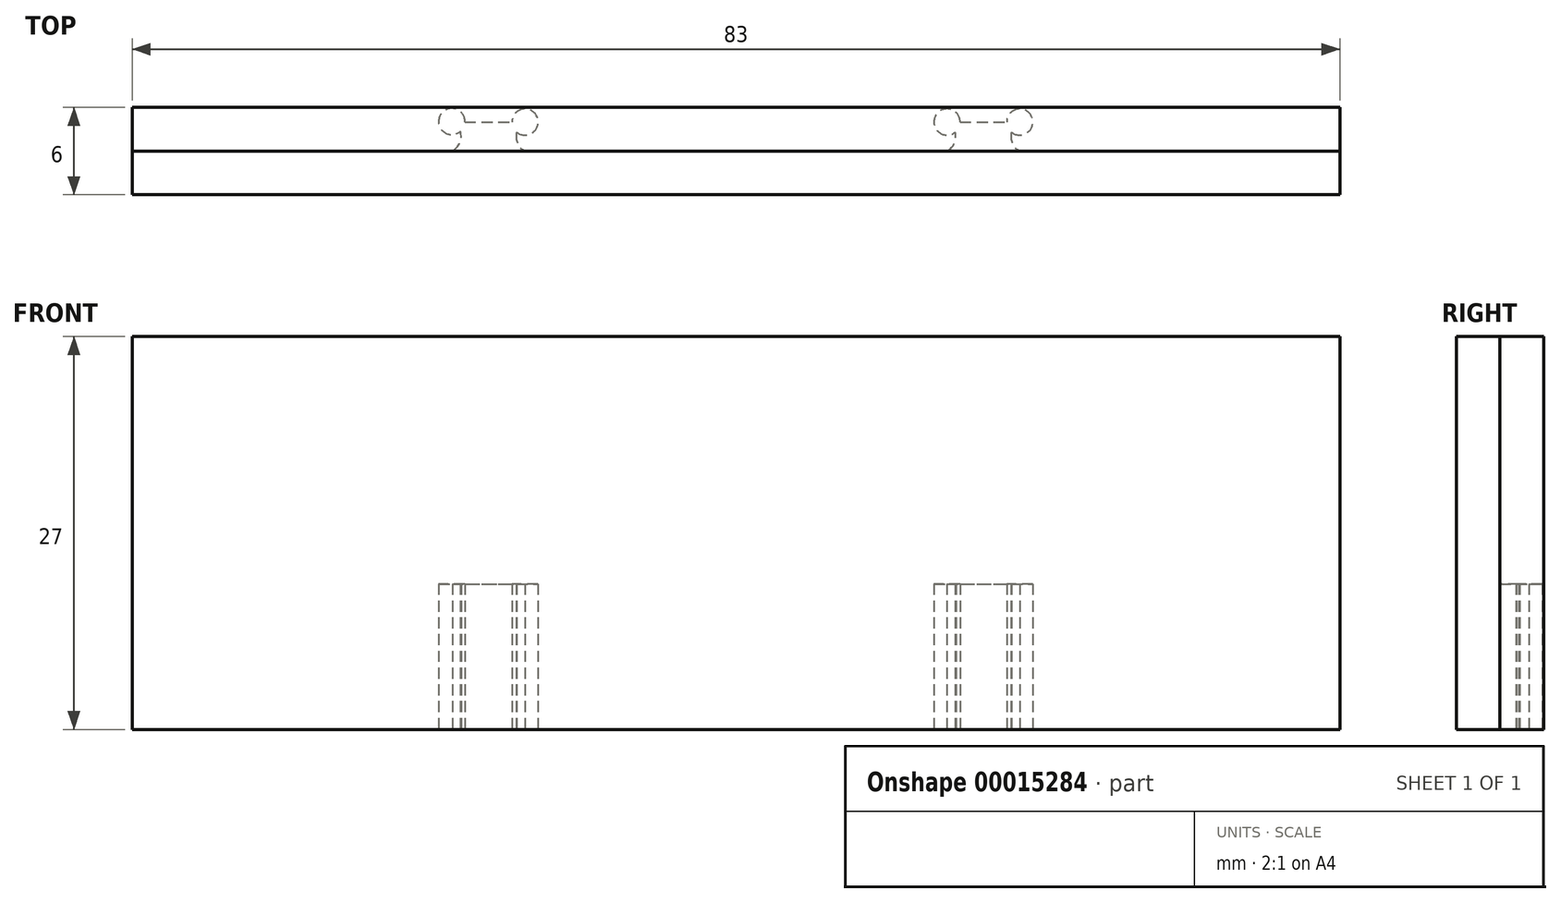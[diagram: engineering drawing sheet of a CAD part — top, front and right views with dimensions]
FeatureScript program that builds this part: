
annotation { "Feature Type Name" : "Feature", "Feature Type Description" : "" }
export const myFeature = defineFeature(function(context is Context, id is Id, definition is map)
    precondition{}
    {
        {
            var Q0;
            Q0=qCreatedBy(makeId("Top.planeOp"),FACE);
            var sketch = newSketch(context, id + "F0", { "sketchPlane" : qUnion([Q0])});
            skLineSegment(sketch, "E0.bottom", {"start": v(0, 0) * mm, "end": v(24.5, 0) * mm});
            skLineSegment(sketch, "E0.top", {"start": v(0, -3) * mm, "end": v(83, -3) * mm});
            skLineSegment(sketch, "E0.left", {"start": v(0, 0) * mm, "end": v(0, -3) * mm});
            skLineSegment(sketch, "E0.right", {"start": v(83, 0) * mm, "end": v(83, -3) * mm});
            skLineSegment(sketch, "E1", {"start": v(0, 2) * mm, "end": v(24.5, 2) * mm, "construction": true});
            skLineSegment(sketch, "E2", {"start": v(24.5, 2) * mm, "end": v(24.5, 0) * mm, "construction": true});
            skLineSegment(sketch, "E3", {"start": v(24.5, 2) * mm, "end": v(27, 2) * mm});
            skLineSegment(sketch, "E4.trimOffspring", {"start": v(27, 0) * mm, "end": v(83, 0) * mm});
            skLineSegment(sketch, "E5", {"start": v(24.5, 0) * mm, "end": v(27, 0) * mm});
            skLineSegment(sketch, "E6.MirrorCS", {"start": v(24.5, 2) * mm, "end": v(22, 2) * mm});
            skLineSegment(sketch, "E7.MirrorCS", {"start": v(24.5, 0) * mm, "end": v(22, 0) * mm});
            skLineSegment(sketch, "E8", {"start": v(83, 2) * mm, "end": v(58.5, 2) * mm, "construction": true});
            skLineSegment(sketch, "E9.1.0.0", {"start": v(58.5, 0) * mm, "end": v(61, 0) * mm});
            skLineSegment(sketch, "E9.1.0.2", {"start": v(58.5, 2) * mm, "end": v(56, 2) * mm});
            skLineSegment(sketch, "E9.1.0.3", {"start": v(58.5, 0) * mm, "end": v(56, 0) * mm});
            skLineSegment(sketch, "E9.1.0.4", {"start": v(58.5, 2) * mm, "end": v(61, 2) * mm});
            skLineSegment(sketch, "E9.1.0.6", {"start": v(58.5, 2) * mm, "end": v(58.5, 0) * mm, "construction": true});
            skLineSegment(sketch, "E9.direction1", {"start": v(24.5, 0) * mm, "end": v(58.5, 0) * mm, "construction": true});
            skLineSegment(sketch, "E10.bottom", {"start": v(0, -3) * mm, "end": v(7.5, -3) * mm});
            skLineSegment(sketch, "E10.top", {"start": v(0, -19) * mm, "end": v(7.5, -19) * mm});
            skLineSegment(sketch, "E10.left", {"start": v(0, -3) * mm, "end": v(0, -19) * mm});
            skLineSegment(sketch, "E10.right", {"start": v(7.5, -3) * mm, "end": v(7.5, -19) * mm});
            skLineSegment(sketch, "E11.bottom", {"start": v(83, -3) * mm, "end": v(75.5, -3) * mm});
            skLineSegment(sketch, "E11.top", {"start": v(83, -19) * mm, "end": v(75.5, -19) * mm});
            skLineSegment(sketch, "E11.left", {"start": v(83, -3) * mm, "end": v(83, -19) * mm});
            skLineSegment(sketch, "E11.right", {"start": v(75.5, -3) * mm, "end": v(75.5, -19) * mm});
            skArc(sketch, "E12", {"start": v(22, 0) * mm, "mid": v(22.6, 1) * mm, "end": v(22, 2) * mm});
            skArc(sketch, "E13.MirrorCS", {"start": v(27, 0) * mm, "mid": v(26.4, 1) * mm, "end": v(27, 2) * mm});
            skArc(sketch, "E14", {"start": v(56, 0) * mm, "mid": v(56.6, 1) * mm, "end": v(56, 2) * mm});
            skArc(sketch, "E15.MirrorCS", {"start": v(61, 0) * mm, "mid": v(60.4, 1) * mm, "end": v(61, 2) * mm});
            skSolve(sketch);
        }
        {
            var Q0;
            Q0=qCreatedBy(makeId("Top.planeOp"),FACE);
            var sketch = newSketch(context, id + "F1", { "sketchPlane" : qUnion([Q0])});
            skLineSegment(sketch, "E16.bottom", {"start": v(0, 0) * mm, "end": v(83, 0) * mm});
            skLineSegment(sketch, "E16.top", {"start": v(0, 3) * mm, "end": v(83, 3) * mm});
            skLineSegment(sketch, "E16.left", {"start": v(0, 0) * mm, "end": v(0, 3) * mm});
            skLineSegment(sketch, "E16.right", {"start": v(83, 0) * mm, "end": v(83, 3) * mm});
            skLineSegment(sketch, "E17.0", {"start": v(24.5, 2) * mm, "end": v(22.87, 2) * mm});
            skLineSegment(sketch, "E18.0", {"start": v(24.5, 2) * mm, "end": v(26.1, 2) * mm});
            skLineSegment(sketch, "E19.0", {"start": v(58.5, 2) * mm, "end": v(56.9, 2) * mm});
            skLineSegment(sketch, "E20.0", {"start": v(58.5, 2) * mm, "end": v(60.1, 2) * mm});
            skCircle(sketch, "E21", {"center": v(21.97, 2.04) * mm, "radius": 0.9 * mm});
            skCircle(sketch, "E22", {"center": v(27, 2) * mm, "radius": 0.9 * mm});
            skCircle(sketch, "E23", {"center": v(56, 2) * mm, "radius": 0.9 * mm});
            skCircle(sketch, "E24", {"center": v(61, 2) * mm, "radius": 0.9 * mm});
            skArc(sketch, "E25.0", {"start": v(22, 0) * mm, "mid": v(22.52, 0.58) * mm, "end": v(22.55, 1.35) * mm});
            skArc(sketch, "E26.0", {"start": v(27, 0) * mm, "mid": v(26.49, 0.55) * mm, "end": v(26.43, 1.3) * mm});
            skArc(sketch, "E27.0", {"start": v(56, 0) * mm, "mid": v(56.51, 0.55) * mm, "end": v(56.57, 1.3) * mm});
            skArc(sketch, "E28.0", {"start": v(61, 0) * mm, "mid": v(60.49, 0.55) * mm, "end": v(60.43, 1.3) * mm});
            skPoint(sketch, "E29.orphan", {"position": v(22, 2) * mm});
            skSolve(sketch);
        }
        {
            var Q0;
            Q0=makeQuery(id+"F0.imprint","IMPRINT",FACE,{"disambiguationData":[TD([[makeQuery(id+"F0.imprint","IMPRINT",EDGE,{"derivedFrom":sQuery(id+"F0.wireOp",EDGE,"E0.bottom")}),-1.0]])]});
            var Q1;
            Q1=makeQuery(id+"F0.imprint","IMPRINT",FACE,{"disambiguationData":[TD([[makeQuery(id+"F0.imprint","IMPRINT",EDGE,{"derivedFrom":sQuery(id+"F0.wireOp",EDGE,"E11.bottom")}),1.0]])]});
            var Q2;
            Q2=makeQuery(id+"F0.imprint","IMPRINT",FACE,{"disambiguationData":[TD([[makeQuery(id+"F0.imprint","IMPRINT",EDGE,{"derivedFrom":sQuery(id+"F0.wireOp",EDGE,"E10.bottom")}),-1.0]])]});
            extrude(context, id + "F2", {"entities" : qUnion([Q0, Q1, Q2]), "depth" : 27 * mm});
        }
        {
            var Q0;
            Q0=makeQuery(id+"F0.imprint","IMPRINT",FACE,{"disambiguationData":[TD([[makeQuery(id+"F0.imprint","IMPRINT",EDGE,{"derivedFrom":sQuery(id+"F0.wireOp",EDGE,"E9.1.0.0")}),1.0]])]});
            var Q1;
            Q1=makeQuery(id+"F0.imprint","IMPRINT",FACE,{"disambiguationData":[TD([[makeQuery(id+"F0.imprint","IMPRINT",EDGE,{"derivedFrom":sQuery(id+"F0.wireOp",EDGE,"E3")}),-1.0]])]});
            extrude(context, id + "F3", {"entities" : qUnion([Q0, Q1]), "operationType" : NewBodyOperationType.ADD, "depth" : 10 * mm});
        }
        {
            var Q0;
            Q0 = qSketchRegion(id + "F1", true);
            var Q1;
            {var subQ1=sQuery(id+"F1.wireOp",EDGE,"6b6c7125-87d3-4553-a127-3a18f75b3079.0");var subQ3=sQuery(id+"F1.wireOp",EDGE,"E18.0");var subQ5=makeQuery(id+"F1.imprint","INTERSECT",VERTEX,{"derivedFrom":[subQ3,subQ1]});Q1=makeQuery(id+"F1.imprint","IMPRINT",FACE,{"disambiguationData":[TD([[makeQuery(id+"F1.imprint","IMPRINT",EDGE,{"disambiguationData":[TD([[subQ5,1.0]])],"derivedFrom":subQ3}),1.0]])]});}
            var Q2;
            {var subQ1=sQuery(id+"F1.wireOp",EDGE,"6b6c7125-87d3-4553-a127-3a18f75b3079.0");var subQ3=sQuery(id+"F1.wireOp",EDGE,"E18.0");var subQ5=makeQuery(id+"F1.imprint","INTERSECT",VERTEX,{"derivedFrom":[subQ3,subQ1]});Q2=makeQuery(id+"F1.imprint","IMPRINT",FACE,{"disambiguationData":[TD([[makeQuery(id+"F1.imprint","IMPRINT",EDGE,{"disambiguationData":[TD([[subQ5,1.0]])],"derivedFrom":subQ3}),-1.0]])]});}
            var Q3;
            {var subQ1=sQuery(id+"F1.wireOp",EDGE,"E17.0");var subQ3=sQuery(id+"F1.wireOp",EDGE,"38192091-4c4b-4ebf-abf7-9709ffb2822d.0");var subQ5=makeQuery(id+"F1.imprint","INTERSECT",VERTEX,{"derivedFrom":[subQ3,subQ1]});Q3=makeQuery(id+"F1.imprint","IMPRINT",FACE,{"disambiguationData":[TD([[makeQuery(id+"F1.imprint","IMPRINT",EDGE,{"disambiguationData":[TD([[subQ5,-1.0]])],"derivedFrom":subQ3}),-1.0]])]});}
            var Q4;
            {var subQ1=sQuery(id+"F1.wireOp",EDGE,"E17.0");var subQ3=sQuery(id+"F1.wireOp",EDGE,"38192091-4c4b-4ebf-abf7-9709ffb2822d.0");var subQ5=makeQuery(id+"F1.imprint","INTERSECT",VERTEX,{"derivedFrom":[subQ3,subQ1]});Q4=makeQuery(id+"F1.imprint","IMPRINT",FACE,{"disambiguationData":[TD([[makeQuery(id+"F1.imprint","IMPRINT",EDGE,{"disambiguationData":[TD([[subQ5,-1.0]])],"derivedFrom":subQ3}),1.0]])]});}
            var Q5;
            {var subQ1=sQuery(id+"F1.wireOp",EDGE,"e493a4b6-5bd2-4034-9364-0e4b5c8cb8ea.0");var subQ3=sQuery(id+"F1.wireOp",EDGE,"E19.0");var subQ5=makeQuery(id+"F1.imprint","INTERSECT",VERTEX,{"derivedFrom":[subQ3,subQ1]});Q5=makeQuery(id+"F1.imprint","IMPRINT",FACE,{"disambiguationData":[TD([[makeQuery(id+"F1.imprint","IMPRINT",EDGE,{"disambiguationData":[TD([[subQ5,1.0]])],"derivedFrom":subQ3}),-1.0]])]});}
            var Q6;
            {var subQ1=sQuery(id+"F1.wireOp",EDGE,"e493a4b6-5bd2-4034-9364-0e4b5c8cb8ea.0");var subQ3=sQuery(id+"F1.wireOp",EDGE,"E19.0");var subQ5=makeQuery(id+"F1.imprint","INTERSECT",VERTEX,{"derivedFrom":[subQ3,subQ1]});Q6=makeQuery(id+"F1.imprint","IMPRINT",FACE,{"disambiguationData":[TD([[makeQuery(id+"F1.imprint","IMPRINT",EDGE,{"disambiguationData":[TD([[subQ5,1.0]])],"derivedFrom":subQ3}),1.0]])]});}
            var Q7;
            {var subQ1=sQuery(id+"F1.wireOp",EDGE,"c7cf41aa-584b-4ac6-8513-ffaf11a8ccd2.0");var subQ3=sQuery(id+"F1.wireOp",EDGE,"E20.0");var subQ5=makeQuery(id+"F1.imprint","INTERSECT",VERTEX,{"derivedFrom":[subQ3,subQ1]});Q7=makeQuery(id+"F1.imprint","IMPRINT",FACE,{"disambiguationData":[TD([[makeQuery(id+"F1.imprint","IMPRINT",EDGE,{"disambiguationData":[TD([[subQ5,1.0]])],"derivedFrom":subQ3}),1.0]])]});}
            var Q8;
            {var subQ1=sQuery(id+"F1.wireOp",EDGE,"c7cf41aa-584b-4ac6-8513-ffaf11a8ccd2.0");var subQ3=sQuery(id+"F1.wireOp",EDGE,"E20.0");var subQ5=makeQuery(id+"F1.imprint","INTERSECT",VERTEX,{"derivedFrom":[subQ3,subQ1]});Q8=makeQuery(id+"F1.imprint","IMPRINT",FACE,{"disambiguationData":[TD([[makeQuery(id+"F1.imprint","IMPRINT",EDGE,{"disambiguationData":[TD([[subQ5,1.0]])],"derivedFrom":subQ3}),-1.0]])]});}
            var Q9;
            {var subQ0=sQuery(id+"F1.wireOp",EDGE,"E25.0");var subQ3=sQuery(id+"F1.wireOp",EDGE,"E17.0");var subQ4=makeQuery(id+"F1.imprint","INTERSECT",VERTEX,{"derivedFrom":[subQ3,subQ0]});Q9=makeQuery(id+"F1.imprint","IMPRINT",FACE,{"disambiguationData":[TD([[makeQuery(id+"F1.imprint","IMPRINT",EDGE,{"disambiguationData":[TD([[subQ4,1.0]])],"derivedFrom":subQ3}),-1.0]])]});}
            var Q10;
            {var subQ0=sQuery(id+"F1.wireOp",EDGE,"E23");var subQ2=makeQuery(id+"F1.imprint","INTERSECT",VERTEX,{"derivedFrom":[sQuery(id+"F1.wireOp",EDGE,"E19.0"),subQ0]});Q10=makeQuery(id+"F1.imprint","IMPRINT",FACE,{"disambiguationData":[TD([[makeQuery(id+"F1.imprint","IMPRINT",EDGE,{"disambiguationData":[TD([[subQ2,-1.0]])],"derivedFrom":subQ0}),1.0]])]});}
            var Q11;
            {var subQ0=sQuery(id+"F1.wireOp",EDGE,"E24");var subQ2=makeQuery(id+"F1.imprint","INTERSECT",VERTEX,{"derivedFrom":[sQuery(id+"F1.wireOp",EDGE,"E20.0"),subQ0]});Q11=makeQuery(id+"F1.imprint","IMPRINT",FACE,{"disambiguationData":[TD([[makeQuery(id+"F1.imprint","IMPRINT",EDGE,{"disambiguationData":[TD([[subQ2,-1.0]])],"derivedFrom":subQ0}),1.0]])]});}
            var Q12;
            {var subQ0=sQuery(id+"F1.wireOp",EDGE,"E21");var subQ2=makeQuery(id+"F1.imprint","INTERSECT",VERTEX,{"derivedFrom":[sQuery(id+"F1.wireOp",EDGE,"E17.0"),subQ0]});Q12=makeQuery(id+"F1.imprint","IMPRINT",FACE,{"disambiguationData":[TD([[makeQuery(id+"F1.imprint","IMPRINT",EDGE,{"disambiguationData":[TD([[subQ2,-1.0]])],"derivedFrom":subQ0}),1.0]])]});}
            var Q13;
            {var subQ0=sQuery(id+"F1.wireOp",EDGE,"E22");var subQ2=makeQuery(id+"F1.imprint","INTERSECT",VERTEX,{"derivedFrom":[sQuery(id+"F1.wireOp",EDGE,"E18.0"),subQ0]});Q13=makeQuery(id+"F1.imprint","IMPRINT",FACE,{"disambiguationData":[TD([[makeQuery(id+"F1.imprint","IMPRINT",EDGE,{"disambiguationData":[TD([[subQ2,-1.0]])],"derivedFrom":subQ0}),1.0]])]});}
            extrude(context, id + "F4", {"entities" : qUnion([Q0, Q1, Q2, Q3, Q4, Q5, Q6, Q7, Q8, Q9, Q10, Q11, Q12, Q13]), "depth" : 27 * mm});
        }
        {
            var Q0;
            {var subQ0=sQuery(id+"F1.wireOp",EDGE,"E23");var subQ2=makeQuery(id+"F1.imprint","INTERSECT",VERTEX,{"derivedFrom":[sQuery(id+"F1.wireOp",EDGE,"E19.0"),subQ0]});Q0=makeQuery(id+"F1.imprint","IMPRINT",FACE,{"disambiguationData":[TD([[makeQuery(id+"F1.imprint","IMPRINT",EDGE,{"disambiguationData":[TD([[subQ2,-1.0]])],"derivedFrom":subQ0}),1.0]])]});}
            var Q1;
            {var subQ0=sQuery(id+"F1.wireOp",EDGE,"E24");var subQ2=makeQuery(id+"F1.imprint","INTERSECT",VERTEX,{"derivedFrom":[sQuery(id+"F1.wireOp",EDGE,"E20.0"),subQ0]});Q1=makeQuery(id+"F1.imprint","IMPRINT",FACE,{"disambiguationData":[TD([[makeQuery(id+"F1.imprint","IMPRINT",EDGE,{"disambiguationData":[TD([[subQ2,-1.0]])],"derivedFrom":subQ0}),1.0]])]});}
            var Q2;
            {var subQ5=sQuery(id+"F1.wireOp",EDGE,"E19.0");Q2=makeQuery(id+"F1.imprint","IMPRINT",FACE,{"disambiguationData":[TD([[makeQuery(id+"F1.imprint","IMPRINT",EDGE,{"derivedFrom":subQ5}),1.0]])]});}
            var Q3;
            {var subQ5=sQuery(id+"F1.wireOp",EDGE,"E17.0");Q3=makeQuery(id+"F1.imprint","IMPRINT",FACE,{"disambiguationData":[TD([[makeQuery(id+"F1.imprint","IMPRINT",EDGE,{"derivedFrom":subQ5}),1.0]])]});}
            var Q4;
            {var subQ0=sQuery(id+"F1.wireOp",EDGE,"E21");var subQ2=makeQuery(id+"F1.imprint","INTERSECT",VERTEX,{"derivedFrom":[sQuery(id+"F1.wireOp",EDGE,"E17.0"),subQ0]});Q4=makeQuery(id+"F1.imprint","IMPRINT",FACE,{"disambiguationData":[TD([[makeQuery(id+"F1.imprint","IMPRINT",EDGE,{"disambiguationData":[TD([[subQ2,-1.0]])],"derivedFrom":subQ0}),1.0]])]});}
            var Q5;
            {var subQ0=sQuery(id+"F1.wireOp",EDGE,"E22");var subQ2=makeQuery(id+"F1.imprint","INTERSECT",VERTEX,{"derivedFrom":[sQuery(id+"F1.wireOp",EDGE,"E18.0"),subQ0]});Q5=makeQuery(id+"F1.imprint","IMPRINT",FACE,{"disambiguationData":[TD([[makeQuery(id+"F1.imprint","IMPRINT",EDGE,{"disambiguationData":[TD([[subQ2,-1.0]])],"derivedFrom":subQ0}),1.0]])]});}
            extrude(context, id + "F5", {"entities" : qUnion([Q0, Q1, Q2, Q3, Q4, Q5]), "operationType" : NewBodyOperationType.REMOVE, "depth" : 10 * mm});
        }
    });
